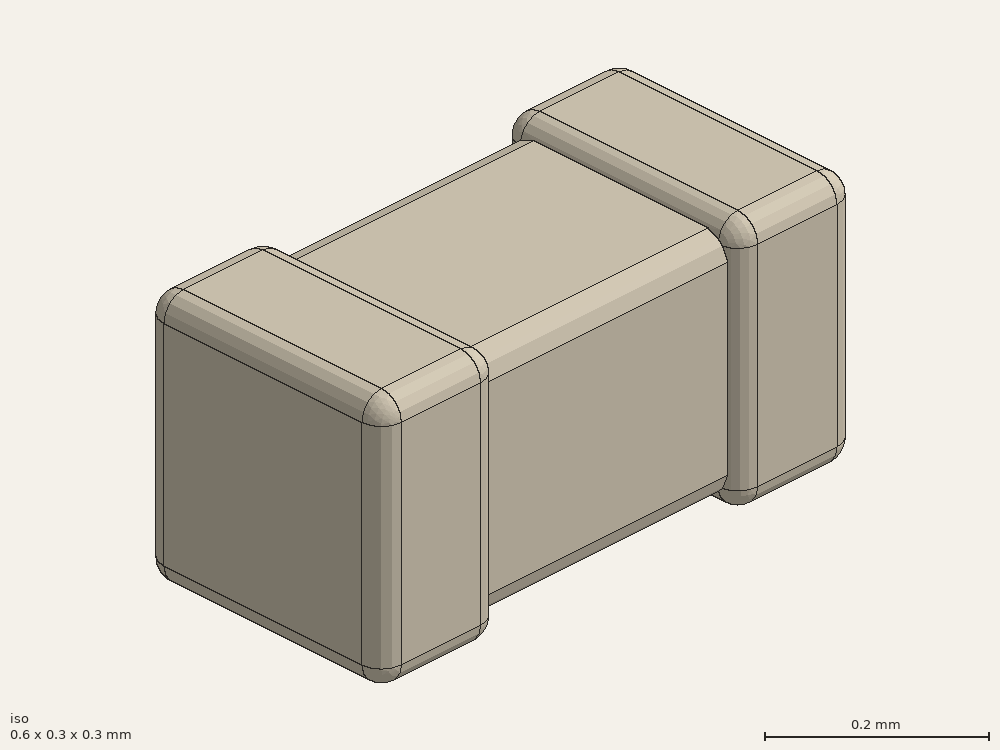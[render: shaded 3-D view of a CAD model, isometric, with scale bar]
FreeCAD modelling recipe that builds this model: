
FCSTD DOCUMENT  (FreeCAD 0.19R17069 (Git))
Label: Kemet Chip Capacitors 0201
License: All rights reserved
LicenseURL: http://en.wikipedia.org/wiki/All_rights_reserved
objects: Sketcher::SketchObject×3, PartDesign::Pad×3, PartDesign::Fillet×3, PartDesign::Body×3, Spreadsheet::Sheet×1, Part::MultiFuse×1
note: 16 computed .brp shape members not serialized (recipe doc carries the construction recipe); baked Part::Feature solids carry a one-line shape summary decoded from their .brp

FEATURE [Spreadsheet::Sheet] Spreadsheet
  cells = C1=eia 0201; A3=length; B3=datasheet; C3(length)==0.6mm; A4=width; B4=datasheet; C4(width)==0.3mm; A5=thickness; B5=datasheet; C5(thickness)==0.3mm; A6=bandwidth; B6=datasheet; C6(bandwidth)==0.15mm; A7=separation; B7=datasheet, minimum; A9=fl; B9=shrink factor length; C9(fl)=0.9; A10=fw; B10=shrink factor width; C10(fw)=0.9; A11=fth; B11=shrink factor thickness; C11(fth)=0.9; A12=filletbody; C12(filletbody)==0.025mm; A13=filletleads; C13(filletleads)==0.025mm
FEATURE [Sketcher::SketchObject] Sketch
  AttachmentOffset = pos=(0,0,0.015) rot=(0,0,1;0rad)
  MapMode = 5
  Placement = pos=(0,0,0.015) rot=(0,0,1;0rad)
  Support = -> [XY_Plane]
  expr: AttachmentOffset.Base.z = (Spreadsheet.thickness - Spreadsheet.thickness * Spreadsheet.fth) / 2
  expr: Constraints[10] = Spreadsheet.width * Spreadsheet.fw
  expr: Constraints[9] = Spreadsheet.length * Spreadsheet.fl
  sketch-geometry (4):
    g0: LineSegment StartX=-0.27 StartY=-0.135 StartZ=0 EndX=0.27 EndY=-0.135 EndZ=0
    g1: LineSegment StartX=0.27 StartY=-0.135 StartZ=0 EndX=0.27 EndY=0.135 EndZ=0
    g2: LineSegment StartX=0.27 StartY=0.135 StartZ=0 EndX=-0.27 EndY=0.135 EndZ=0
    g3: LineSegment StartX=-0.27 StartY=0.135 StartZ=0 EndX=-0.27 EndY=-0.135 EndZ=0
  constraints (11):
    c: Coincident(g0,g1)
    c: Coincident(g1,g2)
    c: Coincident(g2,g3)
    c: Coincident(g3,g0)
    c: Horizontal(g0)
    c: Horizontal(g2)
    c: Vertical(g1)
    c: Vertical(g3)
    c: Symmetric(g0,g1,g-1)
    c: DistanceX(g2,g2) = 0.54
    c: DistanceY(g1,g1) = 0.27
FEATURE [PartDesign::Pad] Pad
  Length = 0.27
  Length2 = 100
  Profile = -> Sketch
  Type = 0
  expr: Length = Spreadsheet.thickness * Spreadsheet.fth
FEATURE [Sketcher::SketchObject] Sketch001
  MapMode = 5
  Placement = pos=(0,0,0) rot=(1,0,0;1.5708rad)
  Support = -> [XZ_Plane001]
  expr: Constraints[12] = Spreadsheet.thickness
  expr: Constraints[10] = Spreadsheet.length / 2
  expr: Constraints[9] = Spreadsheet.bandwidth
  sketch-geometry (4):
    g0: LineSegment StartX=-0.3 StartY=0 StartZ=0 EndX=-0.15 EndY=0 EndZ=0
    g1: LineSegment StartX=-0.15 StartY=0 StartZ=0 EndX=-0.15 EndY=0.3 EndZ=0
    g2: LineSegment StartX=-0.15 StartY=0.3 StartZ=0 EndX=-0.3 EndY=0.3 EndZ=0
    g3: LineSegment StartX=-0.3 StartY=0.3 StartZ=0 EndX=-0.3 EndY=0 EndZ=0
  constraints (13):
    c: Coincident(g0,g1)
    c: Coincident(g1,g2)
    c: Horizontal(g0)
    c: Horizontal(g2)
    c: Vertical(g1)
    c: PointOnObject(g0,g-1)
    c: Coincident(g3,g2)
    c: Coincident(g3,g0)
    c: Vertical(g3)
    c: DistanceX(g2,g2) = 0.15
    c: DistanceX(g2,g-1) = 0.3
    c: DistanceX(g1,g-1) = 0.15
    c: DistanceY(g3,g3) = 0.3
FEATURE [PartDesign::Pad] Pad001
  Length = 0.3
  Length2 = 100
  Midplane = true
  Placement = pos=(0,0,0) rot=(1,0,0;1.5708rad)
  Profile = -> Sketch001
  Type = 0
  expr: Length = Spreadsheet.width
FEATURE [Sketcher::SketchObject] Sketch002
  MapMode = 5
  Placement = pos=(0,0,0) rot=(1,0,0;1.5708rad)
  Support = -> [XZ_Plane002]
  expr: Constraints[11] = Spreadsheet.length / 2
  expr: Constraints[10] = Spreadsheet.thickness
  expr: Constraints[9] = Spreadsheet.bandwidth
  sketch-geometry (4):
    g0: LineSegment StartX=0.15 StartY=0 StartZ=0 EndX=0.3 EndY=0 EndZ=0
    g1: LineSegment StartX=0.3 StartY=0 StartZ=0 EndX=0.3 EndY=0.3 EndZ=0
    g2: LineSegment StartX=0.3 StartY=0.3 StartZ=0 EndX=0.15 EndY=0.3 EndZ=0
    g3: LineSegment StartX=0.15 StartY=0.3 StartZ=0 EndX=0.15 EndY=0 EndZ=0
  constraints (13):
    c: Coincident(g0,g1)
    c: Coincident(g1,g2)
    c: Horizontal(g0)
    c: Horizontal(g2)
    c: Vertical(g1)
    c: PointOnObject(g0,g-1)
    c: Coincident(g3,g2)
    c: Coincident(g3,g0)
    c: Vertical(g3)
    c: DistanceX(g2,g2) = 0.15
    c: DistanceY(g3,g3) = 0.3
    c: DistanceX(g-1,g0) = 0.3
    c: DistanceX(g-1,g2) = 0.15
FEATURE [PartDesign::Pad] Pad002
  Length = 0.3
  Length2 = 100
  Midplane = true
  Placement = pos=(0,0,0) rot=(1,0,0;1.5708rad)
  Profile = -> Sketch002
  Type = 0
  expr: Length = Spreadsheet.width
FEATURE [PartDesign::Fillet] Fillet
  Base = -> Pad001 [Edge8,Edge11,Edge9,Edge6,Edge3,Edge2,Edge1,Edge12,Edge4,Edge7,Edge10,Edge5]
  BaseFeature = -> Pad001
  Placement = pos=(0,0,0) rot=(1,0,0;1.5708rad)
  Radius = 0.025
  expr: Radius = Spreadsheet.filletleads
FEATURE [PartDesign::Body] Body001
  Group = -> [Sketch001,Pad001,Fillet]
  Origin = -> Origin001
  Tip = -> Fillet
FEATURE [PartDesign::Fillet] Fillet001
  Base = -> Pad002 [Edge2,Edge6,Edge7,Edge5,Edge10,Edge9,Edge8,Edge12,Edge4,Edge1,Edge11,Edge3]
  BaseFeature = -> Pad002
  Placement = pos=(0,0,0) rot=(1,0,0;1.5708rad)
  Radius = 0.025
  expr: Radius = Spreadsheet.filletleads
FEATURE [PartDesign::Body] Body002
  Group = -> [Sketch002,Pad002,Fillet001]
  Origin = -> Origin002
  Tip = -> Fillet001
FEATURE [PartDesign::Fillet] Fillet002
  Base = -> Pad [Edge4,Edge10,Edge3,Edge9]
  BaseFeature = -> Pad
  Radius = 0.025
  expr: Radius = Spreadsheet.filletbody
FEATURE [PartDesign::Body] Body
  Group = -> [Sketch,Pad,Fillet002]
  Origin = -> Origin
  Tip = -> Fillet002
FEATURE [Part::MultiFuse] Fusion  label="C_0201_0603M_h0.30"
  Shapes = -> [Body002,Body,Body001]
